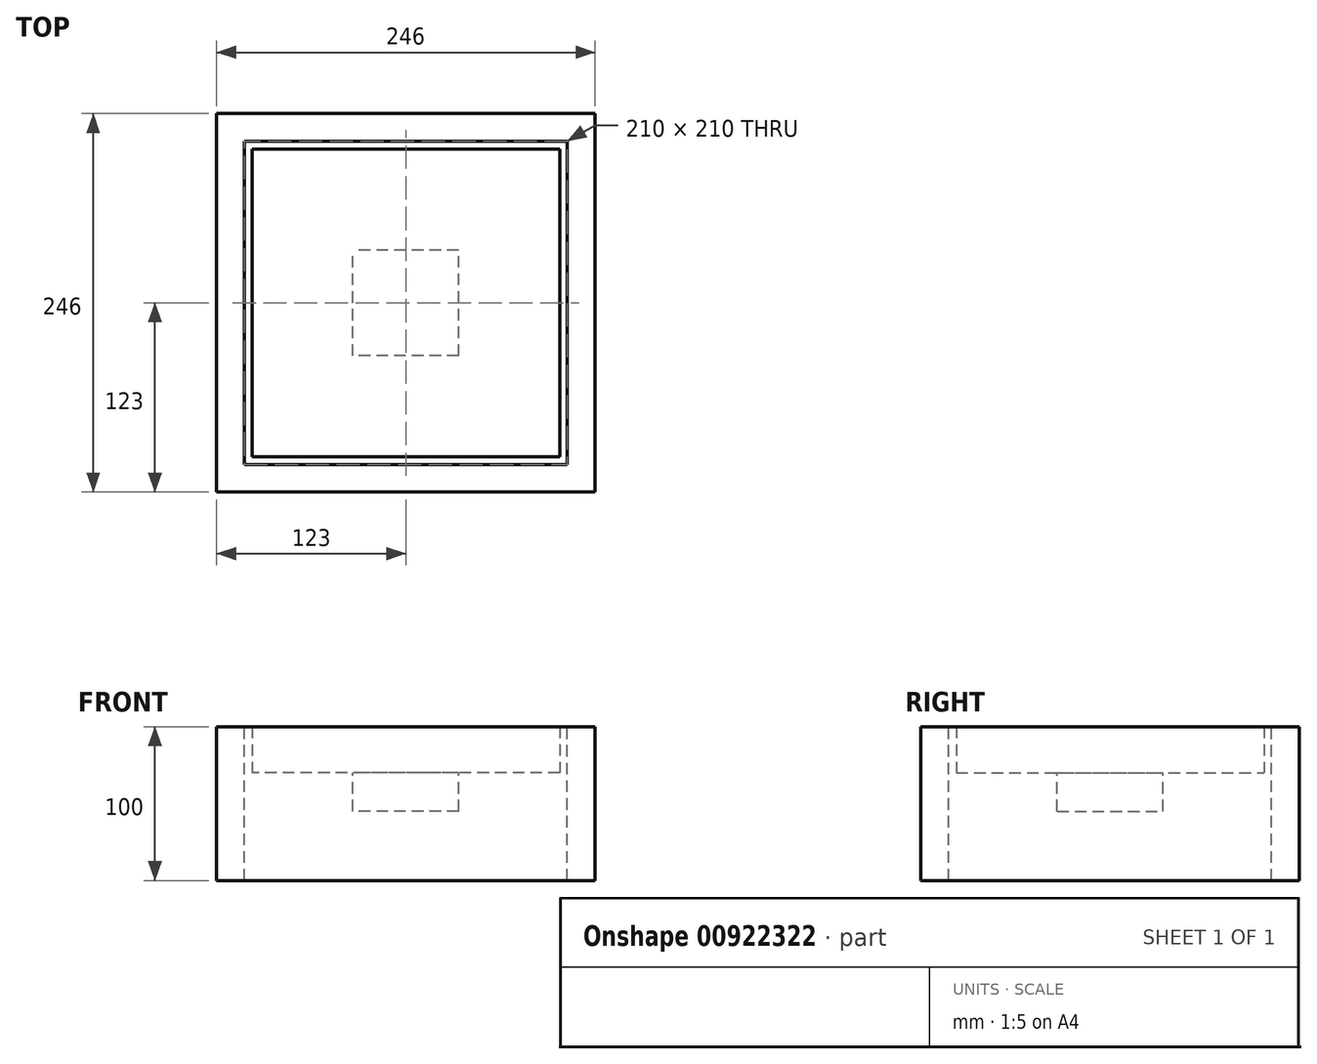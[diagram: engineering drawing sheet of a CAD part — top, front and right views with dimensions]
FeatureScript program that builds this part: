
annotation { "Feature Type Name" : "Feature", "Feature Type Description" : "" }
export const myFeature = defineFeature(function(context is Context, id is Id, definition is map)
    precondition{}
    {
        {
            var Q0;
            Q0=qCreatedBy(makeId("Top.planeOp"),FACE);
            var sketch = newSketch(context, id + "F0", { "sketchPlane" : qUnion([Q0])});
            skLineSegment(sketch, "E0.bottom", {"start": v(100, -100) * mm, "end": v(-100, -100) * mm});
            skLineSegment(sketch, "E0.top", {"start": v(100, 100) * mm, "end": v(-100, 100) * mm});
            skLineSegment(sketch, "E0.left", {"start": v(100, -100) * mm, "end": v(100, 100) * mm});
            skLineSegment(sketch, "E0.right", {"start": v(-100, -100) * mm, "end": v(-100, 100) * mm});
            skPoint(sketch, "E0.middle", {"position": v(0, 0) * mm});
            skSolve(sketch);
        }
        {
            var Q0;
            Q0=makeQuery(id+"F0.imprint","IMPRINT",FACE,{"disambiguationData":[TD([[makeQuery(id+"F0.imprint","IMPRINT",EDGE,{"derivedFrom":sQuery(id+"F0.wireOp",EDGE,"E0.bottom")}),-1.0]])]});
            extrude(context, id + "F1", {"entities" : qUnion([Q0]), "depth" : 30 * mm, "offsetDistance" : 25 * mm});
        }
        {
            var Q0;
            Q0=makeQuery(id+"F1.opExtrude","CAP_FACE",FACE,{"disambiguationData":[OSD([sQuery(id+"F0.wireOp",EDGE,"E0.bottom"),sQuery(id+"F0.wireOp",EDGE,"E0.top"),sQuery(id+"F0.wireOp",EDGE,"E0.left"),sQuery(id+"F0.wireOp",EDGE,"E0.right")])],"isStart":false});
            var sketch = newSketch(context, id + "F2", { "sketchPlane" : qUnion([Q0])});
            skLineSegment(sketch, "E1.0", {"start": v(105, -105) * mm, "end": v(105, 105) * mm});
            skLineSegment(sketch, "E1.1", {"start": v(-105, -105) * mm, "end": v(105, -105) * mm});
            skLineSegment(sketch, "E1.2", {"start": v(-105, 105) * mm, "end": v(-105, -105) * mm});
            skLineSegment(sketch, "E1.3", {"start": v(105, 105) * mm, "end": v(-105, 105) * mm});
            skLineSegment(sketch, "E2.0", {"start": v(123, -123) * mm, "end": v(123, 123) * mm});
            skLineSegment(sketch, "E2.1", {"start": v(-123, -123) * mm, "end": v(123, -123) * mm});
            skLineSegment(sketch, "E2.2", {"start": v(-123, 123) * mm, "end": v(-123, -123) * mm});
            skLineSegment(sketch, "E2.3", {"start": v(123, 123) * mm, "end": v(-123, 123) * mm});
            skSolve(sketch);
        }
        {
            var Q0;
            Q0=makeQuery(id+"F2.imprint","IMPRINT",FACE,{"disambiguationData":[TD([[makeQuery(id+"F2.imprint","IMPRINT",EDGE,{"derivedFrom":sQuery(id+"F2.wireOp",EDGE,"E1.0")}),-1.0]])]});
            extrude(context, id + "F3", {"entities" : qUnion([Q0]), "oppositeDirection" : true, "depth" : 100 * mm, "offsetDistance" : 25 * mm});
        }
        {
            var Q0;
            Q0=makeQuery(id+"F1.opExtrude","CAP_FACE",FACE,{"disambiguationData":[OSD([sQuery(id+"F0.wireOp",EDGE,"E0.bottom"),sQuery(id+"F0.wireOp",EDGE,"E0.top"),sQuery(id+"F0.wireOp",EDGE,"E0.left"),sQuery(id+"F0.wireOp",EDGE,"E0.right")])],"isStart":true});
            var sketch = newSketch(context, id + "F4", { "sketchPlane" : qUnion([Q0])});
            skLineSegment(sketch, "E3.bottom", {"start": v(34.41, 34.41) * mm, "end": v(-34.41, 34.41) * mm});
            skLineSegment(sketch, "E3.top", {"start": v(34.41, -34.41) * mm, "end": v(-34.41, -34.41) * mm});
            skLineSegment(sketch, "E3.left", {"start": v(34.41, 34.41) * mm, "end": v(34.41, -34.41) * mm});
            skLineSegment(sketch, "E3.right", {"start": v(-34.41, 34.41) * mm, "end": v(-34.41, -34.41) * mm});
            skPoint(sketch, "E3.middle", {"position": v(0, 0) * mm});
            skSolve(sketch);
        }
        {
            var Q0;
            Q0=makeQuery(id+"F4.imprint","IMPRINT",FACE,{"disambiguationData":[TD([[makeQuery(id+"F4.imprint","IMPRINT",EDGE,{"derivedFrom":sQuery(id+"F4.wireOp",EDGE,"E3.bottom")}),1.0]])]});
            extrude(context, id + "F5", {"entities" : qUnion([Q0]), "operationType" : NewBodyOperationType.ADD, "depth" : 25 * mm, "offsetDistance" : 25 * mm});
        }
    });
